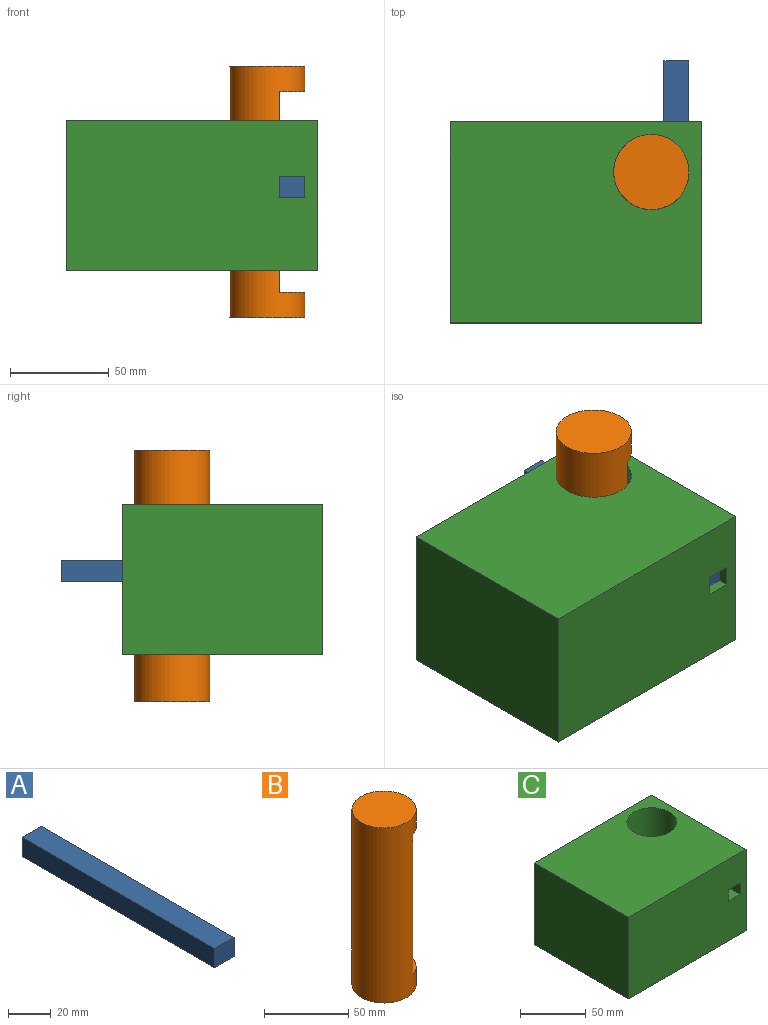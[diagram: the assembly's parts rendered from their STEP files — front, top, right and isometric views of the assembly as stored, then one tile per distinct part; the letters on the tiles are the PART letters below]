
ASSEMBLY  parts=3 mates=2
PART A: 6 faces, bbox 12.6x127x10.9 mm
  f0: plane 127x10.9mm, normal (-1,0,0), area 1384.1mm2, adj f1,f3,f4,f5
  f1: plane 127x12.62mm, normal (0,0,-1), area 1603.2mm2, adj f0,f2,f4,f5
  f2: plane 127x10.9mm, normal (1,0,0), area 1384.1mm2, adj f1,f3,f4,f5
  f3: plane 127x12.62mm, normal (0,0,1), area 1603.2mm2, adj f0,f2,f4,f5
  f4: plane 12.62x10.9mm, normal (0,-1,0), area 137.6mm2, adj f0,f1,f2,f3
  f5: plane 12.62x10.9mm, normal (0,1,0), area 137.6mm2, adj f0,f1,f2,f3
PART B: 6 faces, bbox 38x38x127 mm
  f0: cylinder r=19.01mm len=127mm, axis (0,0,-1), area 10418.1mm2, adj f1,f2,f3,f4,f5
  f1: plane 38.02x38.02mm, normal (0,0,1), area 1135.5mm2, adj f0
  f2: plane 38.02x38.02mm, normal (0,0,-1), area 1135.5mm2, adj f0
  f3: plane 35.84x12.66mm, normal (0,0,-1), area 330.9mm2, adj f0,f4
  f4: plane 101.6x35.84mm, normal (1,0,0), area 3641.4mm2, adj f0,f3,f5
  f5: plane 35.84x12.66mm, normal (0,0,1), area 330.9mm2, adj f0,f4
PART C: 14 faces, bbox 127x101.6x76.2 mm
  f0: plane 127x76.2mm, normal (0,1,0), area 9542.1mm2, adj f2,f3,f4,f5,f7,f9,f10,f13
  f1: plane 127x76.2mm, normal (0,-1,0), area 9542.1mm2, adj f2,f3,f4,f5,f7,f8,f11,f12
  f2: plane 127x101.6mm, normal (0,0,1), area 11763.1mm2, adj f0,f1,f4,f5,f6
  f3: plane 127x101.6mm, normal (0,0,-1), area 11763.1mm2, adj f0,f1,f4,f5,f6
  f4: plane 101.6x76.2mm, normal (1,0,0), area 7741.9mm2, adj f0,f1,f2,f3
  f5: plane 101.6x76.2mm, normal (-1,0,0), area 7741.9mm2, adj f0,f1,f2,f3
  f6: cylinder r=19.05mm len=76.2mm, axis (0,0,-1), area 8620.9mm2, adj f2,f3,f8,f9,f10,f11,f12,f13
  f7: plane 101.6x10.66mm, normal (-1,0,0), area 1082.8mm2, adj f0,f1,f8,f9,f12,f13
  f8: plane 76.2x12.7mm, normal (0,0,-1), area 801.4mm2, adj f1,f6,f7,f11
  f9: plane 25.4x12.7mm, normal (0,0,-1), area 156.2mm2, adj f0,f6,f7,f10
  f10: plane 10.66x7.44mm, normal (1,0,0), area 79.3mm2, adj f0,f6,f9,f13
  f11: plane 58.24x10.66mm, normal (1,0,0), area 620.7mm2, adj f1,f6,f8,f12
  f12: plane 76.2x12.7mm, normal (0,0,1), area 801.4mm2, adj f1,f6,f7,f11
  f13: plane 25.4x12.7mm, normal (0,0,1), area 156.2mm2, adj f0,f6,f7,f10
PLACE A t=(121.69,11.75,28.66)mm
PLACE B t=(115.3,19.02,-32.03)mm
PLACE C t=(13.7,0,-8.36)mm fixed
MATE slider A.f4 <-> C.f1  axis (0,-1,0) through (128,-51.75,39.56)mm
MATE slider B.f0 <-> C.f6  axis (0,0,-1) through (115.3,19.02,94.97)mm
